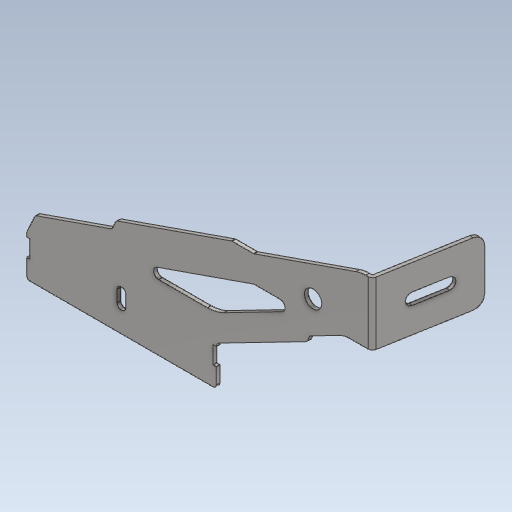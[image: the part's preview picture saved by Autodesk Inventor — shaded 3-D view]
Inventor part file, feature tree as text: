
AUTODESK INVENTOR PART (.ipt)
format: ipt  version: 2020 (Build 240168000, 168)  size: 589,312 bytes
history: native  units: mm
features: other x3, extrude x1, plane x1
ambient origin geometry x8: Origin, YZ Plane, XZ Plane, XY Plane, X Axis, Y Axis, Z Axis, Center Point
bodies: Body1 (feature_tree)
feature tree (5):
  other  "實體1"
  extrude  "擠出1"  Depth=130.0mm
  other  "折彎零件1"
  plane  "工作平面1"
  other  "定義1"
